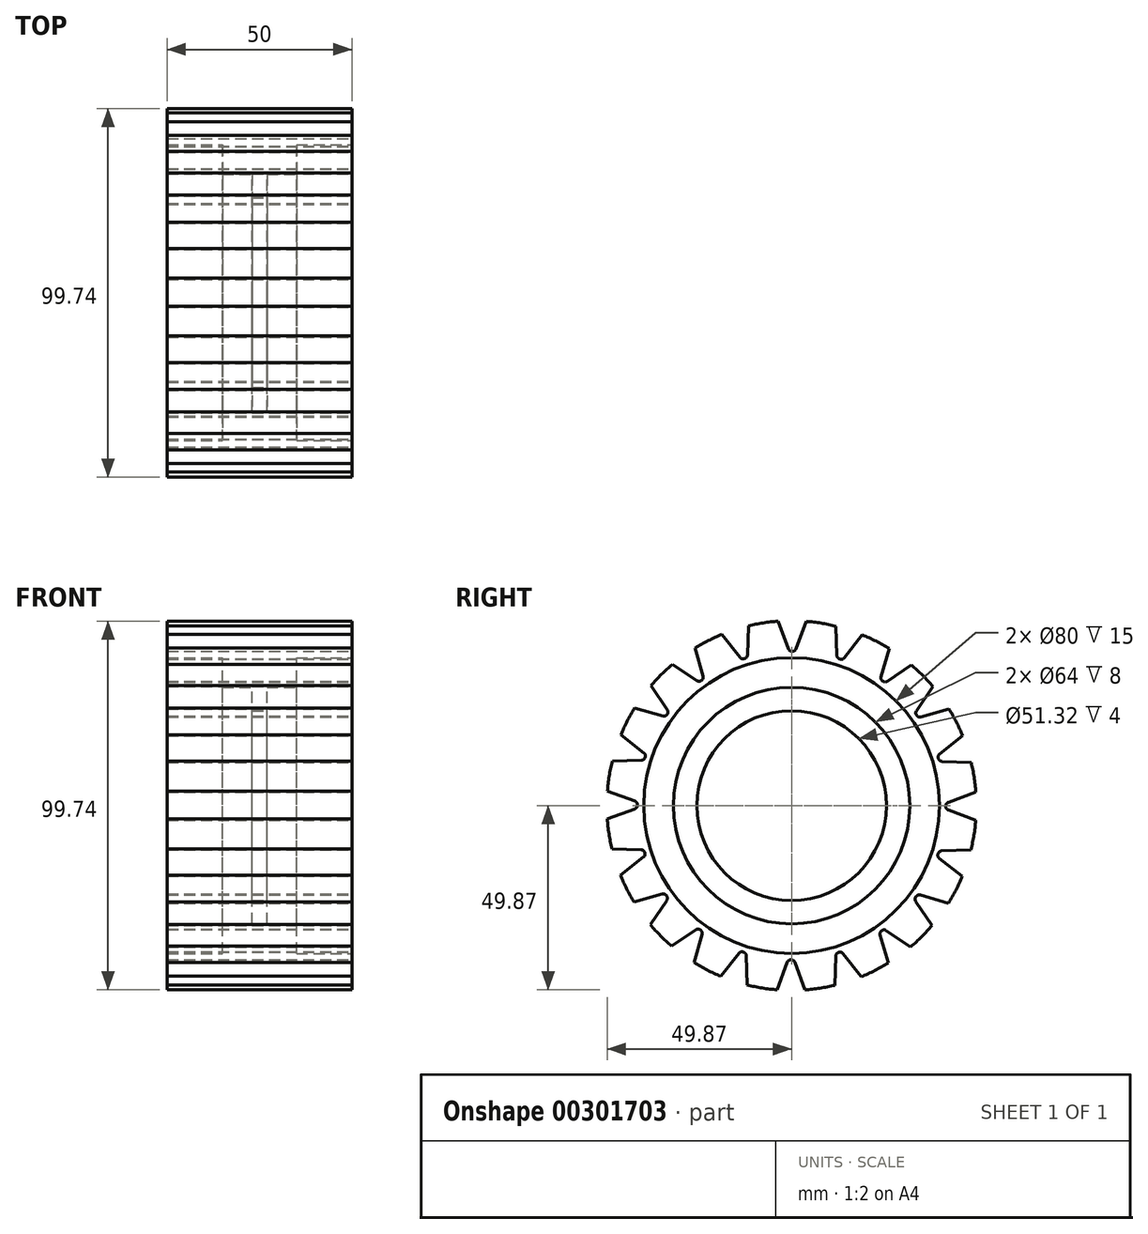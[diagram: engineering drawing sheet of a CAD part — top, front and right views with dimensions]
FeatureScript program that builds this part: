
annotation { "Feature Type Name" : "Feature", "Feature Type Description" : "" }
export const myFeature = defineFeature(function(context is Context, id is Id, definition is map)
    precondition{}
    {
        {
            var Q0;
            Q0=qCreatedBy(makeId("Top.planeOp"),FACE);
            var sketch = newSketch(context, id + "F0", { "sketchPlane" : qUnion([Q0])});
            skLineSegment(sketch, "E0.bottom", {"start": v(0, 0) * mm, "end": v(-50, 0) * mm});
            skLineSegment(sketch, "E0.top", {"start": v(0, 50) * mm, "end": v(-50, 50) * mm});
            skLineSegment(sketch, "E0.left", {"start": v(0, 0) * mm, "end": v(0, 10) * mm});
            skLineSegment(sketch, "E0.right", {"start": v(-50, 0) * mm, "end": v(-50, 10) * mm});
            skLineSegment(sketch, "E1", {"start": v(-50, 50) * mm, "end": v(-50, 40) * mm});
            skLineSegment(sketch, "E2", {"start": v(-50, 40) * mm, "end": v(-35, 40) * mm});
            skLineSegment(sketch, "E3", {"start": v(0, 40) * mm, "end": v(0, 50) * mm});
            skLineSegment(sketch, "E4", {"start": v(-50, 10) * mm, "end": v(-35, 10) * mm});
            skLineSegment(sketch, "E5", {"start": v(0, 10) * mm, "end": v(0, 0) * mm});
            skLineSegment(sketch, "E6", {"start": v(-35, 10) * mm, "end": v(-35, 18) * mm});
            skLineSegment(sketch, "E7", {"start": v(-35, 18) * mm, "end": v(-27, 18) * mm});
            skLineSegment(sketch, "E8", {"start": v(-27, 18) * mm, "end": v(-27, 25.55) * mm});
            skLineSegment(sketch, "E9", {"start": v(-23, 25.55) * mm, "end": v(-23, 18) * mm});
            skLineSegment(sketch, "E10", {"start": v(-23, 18) * mm, "end": v(-15, 18) * mm});
            skLineSegment(sketch, "E11", {"start": v(-15, 18) * mm, "end": v(-15, 10) * mm});
            skLineSegment(sketch, "E12", {"start": v(-15, 10) * mm, "end": v(0, 10) * mm});
            skLineSegment(sketch, "E13", {"start": v(-15, 40) * mm, "end": v(-15, 32) * mm});
            skLineSegment(sketch, "E14", {"start": v(-15, 32) * mm, "end": v(-23, 32) * mm});
            skLineSegment(sketch, "E15", {"start": v(-23, 32) * mm, "end": v(-23, 25.66) * mm});
            skLineSegment(sketch, "E16", {"start": v(-27, 25.66) * mm, "end": v(-27, 32) * mm});
            skLineSegment(sketch, "E17", {"start": v(-27, 32) * mm, "end": v(-35, 32) * mm});
            skLineSegment(sketch, "E18", {"start": v(-35, 32) * mm, "end": v(-35, 40) * mm});
            skLineSegment(sketch, "E19.trimOffspring", {"start": v(-50, 40) * mm, "end": v(-50, 50) * mm});
            skLineSegment(sketch, "E20.trimOffspring", {"start": v(-15, 40) * mm, "end": v(0, 40) * mm});
            skLineSegment(sketch, "E21", {"start": v(-27, 25.66) * mm, "end": v(-23, 25.66) * mm});
            skSolve(sketch);
        }
        {
            var Q0;
            Q0 = qSketchRegion(id + "F0", true);
            var Q1;
            Q1=sQuery(id+"F0.wireOp",EDGE,"E0.bottom");
            revolve(context, id + "F1", {"entities" : qUnion([Q0]), "axis" : qUnion([Q1]), "revolveType" : RevolveType.FULL});
        }
        {
            var Q0;
            Q0=makeQuery(id+"F1.opRevolve","SWEPT_FACE",FACE,{"disambiguationData":[OSD([sQuery(id+"F0.wireOp",EDGE,"E3")])]});
            var sketch = newSketch(context, id + "F2", { "sketchPlane" : qUnion([Q0])});
            skLineSegment(sketch, "E22", {"start": v(0, 0) * mm, "end": v(0, 50.02) * mm, "construction": true});
            skCircle(sketch, "E23.0.0", {"center": v(0, 0) * mm, "radius": 50 * mm});
            skLineSegment(sketch, "E24", {"start": v(1.2, 42.4) * mm, "end": v(3.91, 49.85) * mm});
            skLineSegment(sketch, "E25", {"start": v(-0.87, 42.4) * mm, "end": v(-3.6, 49.87) * mm});
            skLineSegment(sketch, "E26", {"start": v(0.07, 41.74) * mm, "end": v(0.26, 41.74) * mm});
            skPoint(sketch, "E27.visualSharp", {"position": v(-0.63, 41.74) * mm});
            skArc(sketch, "E27.filletArc", {"start": v(-0.87, 42.4) * mm, "mid": v(-0.5, 41.92) * mm, "end": v(0.07, 41.74) * mm});
            skPoint(sketch, "E28.visualSharp", {"position": v(0.96, 41.74) * mm});
            skArc(sketch, "E28.filletArc", {"start": v(0.26, 41.74) * mm, "mid": v(0.84, 41.92) * mm, "end": v(1.2, 42.4) * mm});
            skSolve(sketch);
        }
        {
            var Q0;
            {var subQ1=sQuery(id+"F2.wireOp",EDGE,"E24");Q0=makeQuery(id+"F2.imprint","IMPRINT",FACE,{"disambiguationData":[TD([[makeQuery(id+"F2.imprint","IMPRINT",EDGE,{"derivedFrom":subQ1}),1.0]])]});}
            extrude(context, id + "F3", {"entities" : qUnion([Q0]), "operationType" : NewBodyOperationType.REMOVE, "oppositeDirection" : true, "depth" : 50 * mm});
        }
        {
            var Q0;
            Q0=makeQuery(id+"F3.boolean.opBoolean","COPY",FACE,{"derivedFrom":makeQuery(id+"F3.opExtrude","SWEPT_FACE",FACE,{"disambiguationData":[OSD([sQuery(id+"F2.wireOp",EDGE,"E24")])]})});
            var Q1;
            Q1=makeQuery(id+"F3.boolean.opBoolean","COPY",FACE,{"derivedFrom":makeQuery(id+"F3.opExtrude","SWEPT_FACE",FACE,{"disambiguationData":[OSD([sQuery(id+"F2.wireOp",EDGE,"E28.filletArc")])]})});
            var Q2;
            Q2=makeQuery(id+"F3.boolean.opBoolean","COPY",FACE,{"derivedFrom":makeQuery(id+"F3.opExtrude","SWEPT_FACE",FACE,{"disambiguationData":[OSD([sQuery(id+"F2.wireOp",EDGE,"E26")])]})});
            var Q3;
            Q3=makeQuery(id+"F3.boolean.opBoolean","COPY",FACE,{"derivedFrom":makeQuery(id+"F3.opExtrude","SWEPT_FACE",FACE,{"disambiguationData":[OSD([sQuery(id+"F2.wireOp",EDGE,"E27.filletArc")])]})});
            var Q4;
            Q4=makeQuery(id+"F3.boolean.opBoolean","COPY",FACE,{"derivedFrom":makeQuery(id+"F3.opExtrude","SWEPT_FACE",FACE,{"disambiguationData":[OSD([sQuery(id+"F2.wireOp",EDGE,"E25")])]})});
            var Q5;
            Q5=makeQuery(id+"F1.opRevolve","SWEPT_FACE",FACE,{"disambiguationData":[OSD([sQuery(id+"F0.wireOp",EDGE,"E0.top")])]});
            circularPattern(context, id + "F4", {"patternType" : PatternType.FACE, "operationType" : NewBodyOperationType.REMOVE, "faces" : qUnion([Q0, Q1, Q2, Q3, Q4]), "axis" : qUnion([Q5]), "angle" : 360 * degree, "instanceCount" : 20, "equalSpace" : true});
        }
    });
